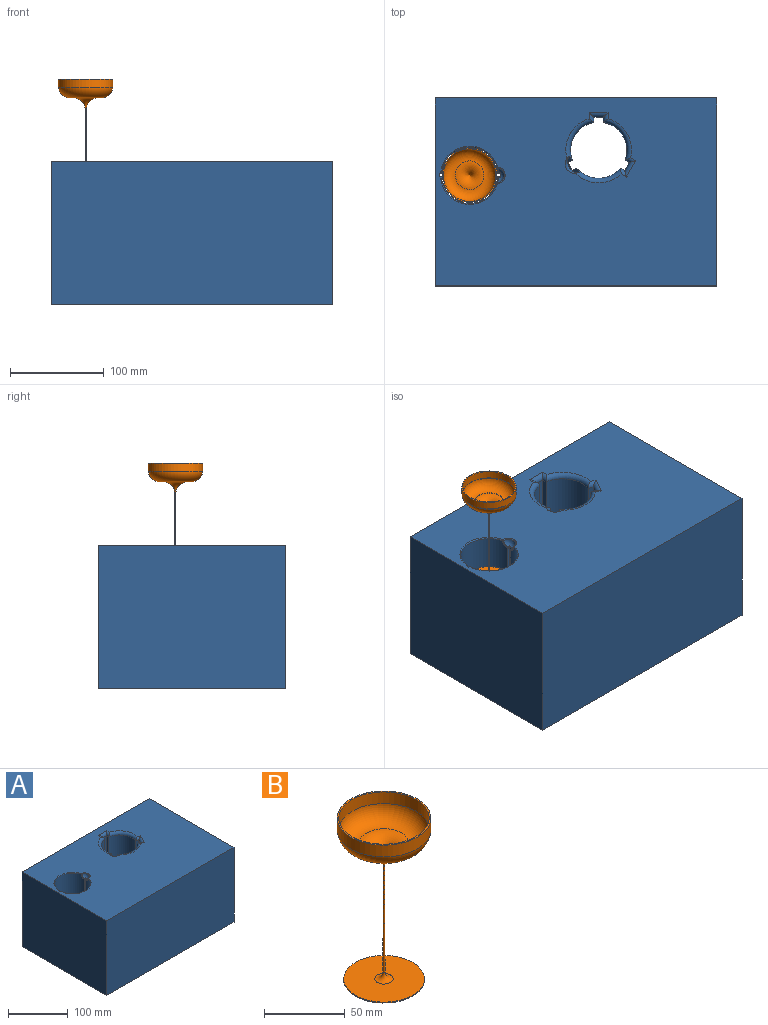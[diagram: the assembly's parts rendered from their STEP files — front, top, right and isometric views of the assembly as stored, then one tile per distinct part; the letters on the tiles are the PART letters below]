
ASSEMBLY  parts=2 mates=1
PART A: 48 faces, bbox 300.1x200.1x153.4 mm
  f0: cylinder r=30mm len=147.4mm, axis (0,0,-1), area 7780.5mm2, adj f1,f10,f25,f43
  f1: plane 150.31x4.76mm, normal (-0.5,0.87,0), area 803.2mm2, adj f0,f2,f25,f37,f43
  f2: plane 145.71x8.66mm, normal (0.87,0.5,0), area 1457.1mm2, adj f1,f3,f25,f37
  f3: plane 150.31x4.76mm, normal (0.5,-0.87,0), area 803.2mm2, adj f2,f4,f25,f37,f39
  f4: cylinder r=30mm len=147.4mm, axis (0,0,-1), area 7780.5mm2, adj f3,f11,f25,f39
  f5: plane 144.58x2.41mm, normal (0,-1,0), area 347.1mm2, adj f20,f21,f25,f33,f34
  f6: plane 144.58x2.41mm, normal (0,1,0), area 347.1mm2, adj f16,f21,f25,f30,f31
  f7: plane 300x152.4mm, normal (0,1,0), area 45720mm2, adj f8,f23,f24,f25
  f8: plane 200x152.4mm, normal (-1,0,0), area 30480mm2, adj f7,f9,f24,f25
  f9: plane 300x152.4mm, normal (0,-1,0), area 45720mm2, adj f8,f23,f24,f25
  f10: plane 147.4x4.69mm, normal (0.5,0.87,0), area 798.8mm2, adj f0,f22,f25,f45
  f11: plane 147.4x5.42mm, normal (1,0,0), area 798.8mm2, adj f4,f12,f25,f40
  f12: plane 147.4x10mm, normal (0,-1,0), area 1474mm2, adj f11,f13,f25,f41
  f13: plane 147.4x5.42mm, normal (-1,0,0), area 798.8mm2, adj f12,f14,f25,f42
  f14: cylinder r=30mm len=147.4mm, axis (0,0,-1), area 7780.5mm2, adj f13,f15,f25,f44
  f15: plane 147.4x4.69mm, normal (-0.5,-0.87,0), area 798.8mm2, adj f14,f22,f25,f46
  f16: cylinder r=30mm len=151.4mm, axis (0,0,-1), area 13690.3mm2, adj f6,f17,f25,f28,f30
  f17: plane 152.42x2.43mm, normal (0,1,0), area 366.6mm2, adj f16,f18,f24,f25,f28
  f18: plane 152.4x3.65mm, normal (1,0,0), area 555.9mm2, adj f17,f19,f24,f25
  f19: plane 152.42x2.43mm, normal (0,-1,0), area 366.6mm2, adj f18,f20,f24,f25,f36
  f20: cylinder r=30mm len=151.4mm, axis (0,0,-1), area 13690.3mm2, adj f5,f19,f25,f34,f36
  f21: plane 144.79x3.69mm, normal (-1,0,0), area 527.6mm2, adj f5,f6,f25,f31,f32,f33
  f22: plane 147.4x8.66mm, normal (-0.87,0.5,0), area 1474mm2, adj f10,f15,f25,f47
  f23: plane 200x152.4mm, normal (1,0,0), area 30480mm2, adj f7,f9,f24,f25
  f24: plane 300x200mm, normal (0,0,1), area 52752.6mm2, adj f7,f8,f9,f17,f18,f19,f23,f27
  f25: plane 300x200mm, normal (0,0,-1), area 54173.7mm2, adj f0,f1,f2,f3,f4,f5,f6,f7
  f26: sphere r=8mm, area 135.6mm2, adj f27,f30,f31,f32,f33,f34
  f27: torus R=8.94mm, axis (0,0,1), area 36.1mm2, adj f24,f26,f29,f35
  f28: torus R=31mm, axis (0,0,1), area 133.1mm2, adj f16,f17,f24,f29
  f29: sphere r=1mm, area 1.8mm2, adj f27,f28,f30
  f30: bspline ~9.62x8.03mm, area 12.5mm2, adj f6,f16,f26,f29,f31
  f31: torus R=8.55mm, axis (0,1,0), area 3.1mm2, adj f6,f21,f26,f30,f32
  f32: torus R=7.83mm, axis (1,0,0), area 4.7mm2, adj f21,f26,f31,f33
  f33: torus R=8.55mm, axis (0,1,0), area 3.1mm2, adj f5,f21,f26,f32,f34
  f34: bspline ~9.62x8.03mm, area 12.5mm2, adj f5,f20,f26,f33,f35
  f35: sphere r=1mm, area 1.8mm2, adj f27,f34,f36
  f36: torus R=31mm, axis (0,0,1), area 133.1mm2, adj f19,f20,f24,f35
  f37: plane 17.8x12.46mm, normal (-0.61,-0.35,0.71), area 60.3mm2, adj f1,f2,f3,f38,f39,f43
  f38: torus R=1.2mm, axis (-0.5,0.87,0), area 175.2mm2, adj f24,f37,f39,f43
  f39: torus R=35mm, axis (0,0,1), area 405.9mm2, adj f3,f4,f24,f37,f38,f40
  f40: cylinder r=5mm len=10.42mm, axis (0,-1,0), area 46.6mm2, adj f11,f24,f39,f41
  f41: cylinder r=5mm len=20mm, axis (-1,0,0), area 117.8mm2, adj f12,f24,f40,f42
  f42: cylinder r=5mm len=10.42mm, axis (0,1,0), area 46.6mm2, adj f13,f24,f41,f44
  f43: torus R=35mm, axis (0,0,1), area 405.9mm2, adj f0,f1,f24,f37,f38,f45
  f44: torus R=35mm, axis (0,0,1), area 408.3mm2, adj f14,f24,f42,f46
  f45: cylinder r=5mm len=11.52mm, axis (0.87,-0.5,0), area 46.6mm2, adj f10,f24,f43,f47
  f46: cylinder r=5mm len=11.52mm, axis (-0.87,0.5,0), area 46.6mm2, adj f15,f24,f44,f47
  f47: cylinder r=5mm len=19.82mm, axis (0.5,0.87,0), area 117.8mm2, adj f22,f24,f45,f46
PART B: 12 faces, bbox 63x63x122.4 mm
  f0: plane 58x58mm, normal (0,0,1), area 179.1mm2, adj f1,f11
  f1: cylinder r=29mm len=58mm, axis (0,0,-1), area 1626mm2, adj f0,f2
  f2: torus R=16.61mm, axis (0,0,-1), area 2908.5mm2, adj f1,f3
  f3: torus R=13.5mm, axis (0,0,-1), area 813.1mm2, adj f2,f4
  f4: cone r=0.51mm half-angle=0.1deg, axis (0,0,-1), area 306.2mm2, adj f3,f5
  f5: torus R=5.65mm, axis (0,0,-1), area 121.7mm2, adj f4,f6
  f6: plane 50x50mm, normal (0,0,1), area 1863.2mm2, adj f5,f7
  f7: cylinder r=25mm len=50mm, axis (0,0,-1), area 105.1mm2, adj f6,f8
  f8: plane 50x50mm, normal (0,0,-1), area 1963.5mm2, adj f7
  f9: torus R=13.5mm, axis (0,0,-1), area 796mm2, adj f10
  f10: torus R=16.61mm, axis (0,0,-1), area 2602.1mm2, adj f9,f11
  f11: cylinder r=28mm len=56mm, axis (0,0,-1), area 1559.4mm2, adj f0,f10
PLACE A t=(-182.57,12.08,7.31)mm fixed
PLACE B rot(axis=(0,0,1),12.2deg) t=(-259.25,52.6,247.74)mm
MATE cylindrical A.f16 <-> B.f1  axis (0,0,-1) through (-259.25,52.6,158.71)mm
